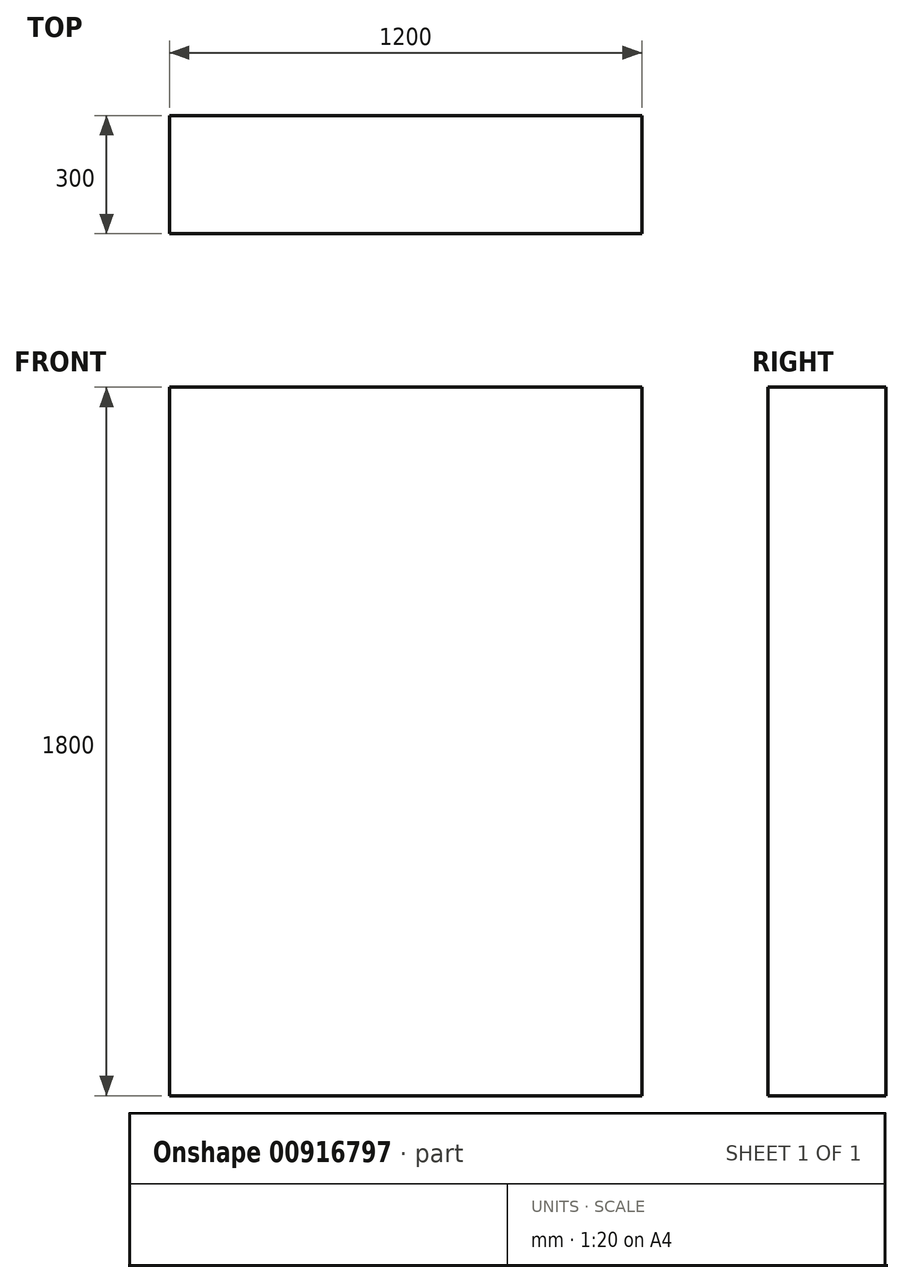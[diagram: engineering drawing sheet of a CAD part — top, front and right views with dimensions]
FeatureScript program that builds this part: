
annotation { "Feature Type Name" : "Feature", "Feature Type Description" : "" }
export const myFeature = defineFeature(function(context is Context, id is Id, definition is map)
    precondition{}
    {
        {
            var Q0;
            Q0=qCreatedBy(makeId("Top.planeOp"),FACE);
            var sketch = newSketch(context, id + "F0", { "sketchPlane" : qUnion([Q0])});
            skLineSegment(sketch, "E0.bottom", {"start": v(600, -150) * mm, "end": v(-600, -150) * mm});
            skLineSegment(sketch, "E0.top", {"start": v(600, 150) * mm, "end": v(-600, 150) * mm});
            skLineSegment(sketch, "E0.left", {"start": v(600, -150) * mm, "end": v(600, 150) * mm});
            skLineSegment(sketch, "E0.right", {"start": v(-600, -150) * mm, "end": v(-600, 150) * mm});
            skPoint(sketch, "E0.middle", {"position": v(0, 0) * mm});
            skSolve(sketch);
        }
        {
            var Q0;
            Q0 = qSketchRegion(id + "F0", true);
            extrude(context, id + "F1", {"entities" : qUnion([Q0]), "depth" : 1800 * mm, "offsetDistance" : 25 * mm});
        }
    });
